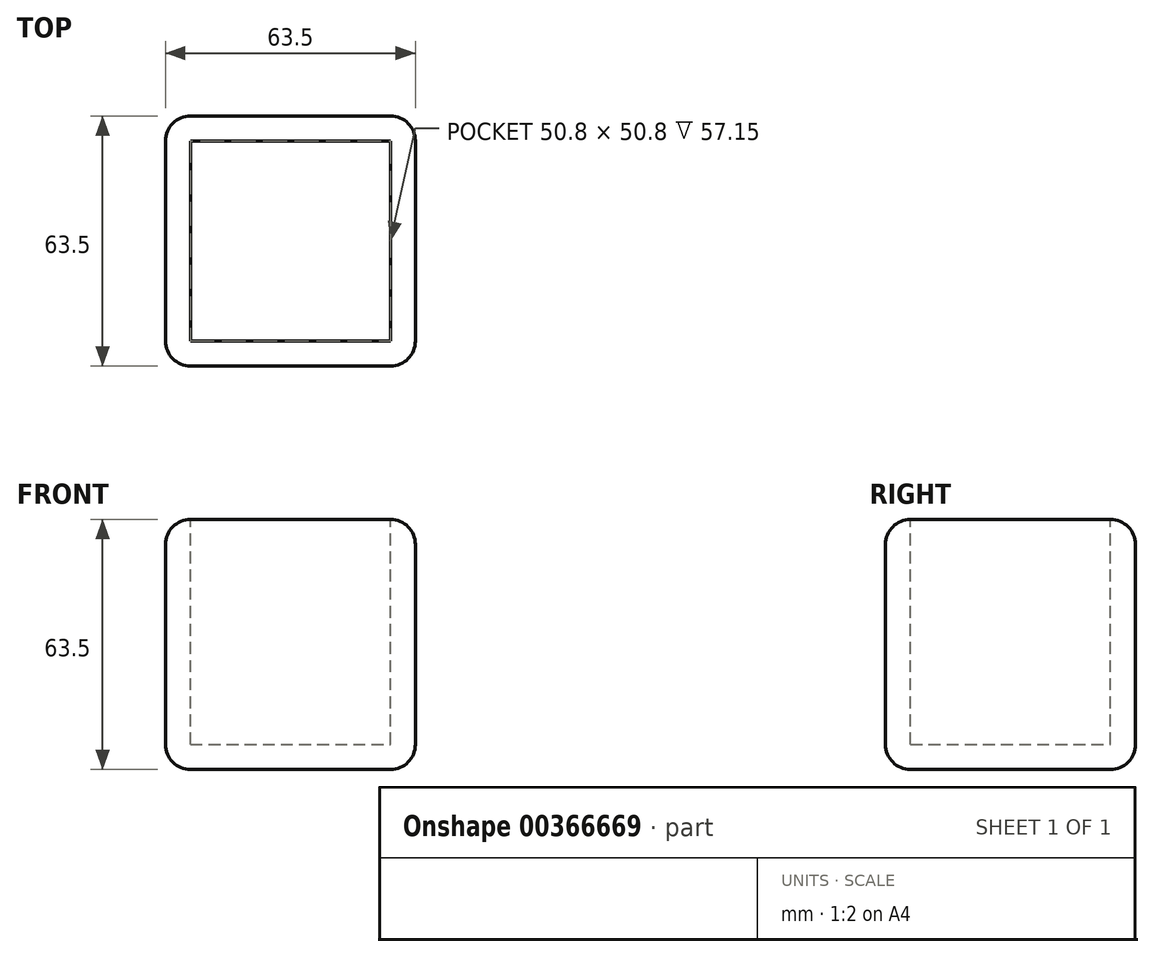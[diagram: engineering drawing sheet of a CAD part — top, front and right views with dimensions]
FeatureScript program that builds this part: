
annotation { "Feature Type Name" : "Feature", "Feature Type Description" : "" }
export const myFeature = defineFeature(function(context is Context, id is Id, definition is map)
    precondition{}
    {
        {
            var Q0;
            Q0=qCreatedBy(makeId("Front.planeOp"),FACE);
            var sketch = newSketch(context, id + "F0", { "sketchPlane" : qUnion([Q0])});
            skLineSegment(sketch, "E0", {"start": v(-69.43, 0) * mm, "end": v(-69.43, 63.5) * mm});
            skLineSegment(sketch, "E1", {"start": v(-69.43, 63.5) * mm, "end": v(-5.93, 63.5) * mm});
            skLineSegment(sketch, "E2", {"start": v(-5.93, 63.5) * mm, "end": v(-5.93, 0) * mm});
            skLineSegment(sketch, "E3", {"start": v(-5.93, 0) * mm, "end": v(-69.43, 0) * mm});
            skSolve(sketch);
        }
        {
            var Q0;
            Q0=makeQuery(id+"F0.imprint","IMPRINT",FACE,{"disambiguationData":[TD([[makeQuery(id+"F0.imprint","IMPRINT",EDGE,{"derivedFrom":sQuery(id+"F0.wireOp",EDGE,"E0")}),-1.0]])]});
            extrude(context, id + "F1", {"entities" : qUnion([Q0]), "depth" : 63.5 * mm});
        }
        {
            var Q0;
            Q0=makeQuery(id+"F1.opExtrude","SWEPT_FACE",FACE,{"disambiguationData":[OSD([sQuery(id+"F0.wireOp",EDGE,"E3")])]});
            var Q1;
            Q1=makeQuery(id+"F1.opExtrude","CAP_FACE",FACE,{"disambiguationData":[OSD([sQuery(id+"F0.wireOp",EDGE,"E0"),sQuery(id+"F0.wireOp",EDGE,"E1"),sQuery(id+"F0.wireOp",EDGE,"E2"),sQuery(id+"F0.wireOp",EDGE,"E3")])],"isStart":false});
            var Q2;
            Q2=makeQuery(id+"F1.opExtrude","SWEPT_FACE",FACE,{"disambiguationData":[OSD([sQuery(id+"F0.wireOp",EDGE,"E2")])]});
            var Q3;
            Q3=makeQuery(id+"F1.opExtrude","CAP_FACE",FACE,{"disambiguationData":[OSD([sQuery(id+"F0.wireOp",EDGE,"E0"),sQuery(id+"F0.wireOp",EDGE,"E1"),sQuery(id+"F0.wireOp",EDGE,"E2"),sQuery(id+"F0.wireOp",EDGE,"E3")])],"isStart":true});
            var Q4;
            Q4=makeQuery(id+"F1.opExtrude","SWEPT_FACE",FACE,{"disambiguationData":[OSD([sQuery(id+"F0.wireOp",EDGE,"E0")])]});
            fillet(context, id + "F2", {"entities" : qUnion([Q0, Q1, Q2, Q3, Q4]), "radius" : 6.35 * mm, "tangentPropagation" : true, "allowEdgeOverflow" : false});
        }
        {
            var Q0;
            Q0=makeQuery(id+"F1.opExtrude","SWEPT_FACE",FACE,{"disambiguationData":[OSD([sQuery(id+"F0.wireOp",EDGE,"E1")])]});
            var sketch = newSketch(context, id + "F3", { "sketchPlane" : qUnion([Q0])});
            skLineSegment(sketch, "E4.bottom", {"start": v(-63.08, -6.35) * mm, "end": v(-12.28, -6.35) * mm});
            skLineSegment(sketch, "E4.top", {"start": v(-63.08, -57.15) * mm, "end": v(-12.28, -57.15) * mm});
            skLineSegment(sketch, "E4.left", {"start": v(-63.08, -6.35) * mm, "end": v(-63.08, -57.15) * mm});
            skLineSegment(sketch, "E4.right", {"start": v(-12.28, -6.35) * mm, "end": v(-12.28, -57.15) * mm});
            skSolve(sketch);
        }
        {
            var Q0;
            Q0=makeQuery(id+"F3.imprint","IMPRINT",FACE,{"disambiguationData":[TD([[makeQuery(id+"F3.imprint","IMPRINT",EDGE,{"derivedFrom":sQuery(id+"F3.wireOp",EDGE,"E4.bottom")}),1.0]])]});
            extrude(context, id + "F4", {"entities" : qUnion([Q0]), "operationType" : NewBodyOperationType.REMOVE, "oppositeDirection" : true, "depth" : 57.15 * mm});
        }
    });
